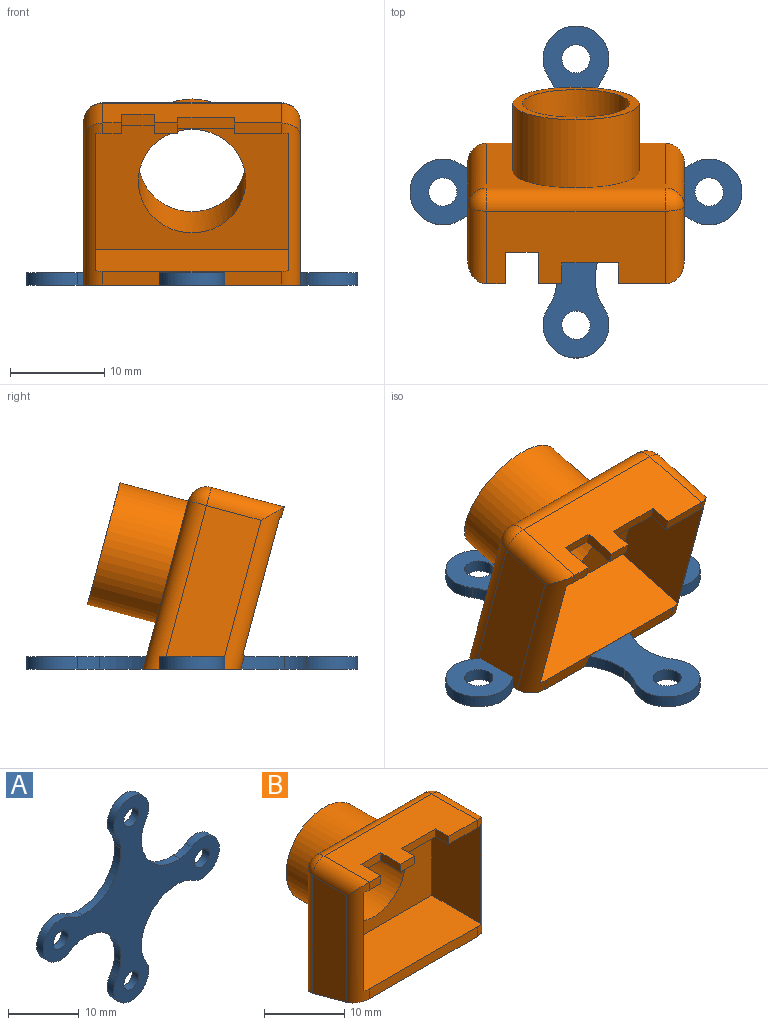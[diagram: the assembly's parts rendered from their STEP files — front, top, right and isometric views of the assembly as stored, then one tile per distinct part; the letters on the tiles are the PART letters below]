
ASSEMBLY  parts=2 mates=1
PART A: 22 faces, bbox 35.3x1.3x35.3 mm
  f0: cylinder r=5mm len=2.39mm, axis (0,1,0), area 3.3mm2, adj f1,f19,f20,f21
  f1: cylinder r=3.5mm len=7mm, axis (0,1,0), area 19.7mm2, adj f0,f2,f20,f21
  f2: cylinder r=5mm len=2.39mm, axis (0,1,0), area 3.3mm2, adj f1,f3,f20,f21
  f3: cylinder r=7.18mm len=7.75mm, axis (0,1,0), area 16.1mm2, adj f2,f4,f20,f21
  f4: cylinder r=5mm len=2.39mm, axis (0,1,0), area 3.3mm2, adj f3,f5,f20,f21
  f5: cylinder r=3.5mm len=7mm, axis (0,1,0), area 19.7mm2, adj f4,f6,f20,f21
  f6: cylinder r=5mm len=2.39mm, axis (0,1,0), area 3.3mm2, adj f5,f7,f20,f21
  f7: cylinder r=7.18mm len=7.75mm, axis (0,1,0), area 16.1mm2, adj f6,f8,f20,f21
  f8: cylinder r=5mm len=2.39mm, axis (0,1,0), area 3.3mm2, adj f7,f9,f20,f21
  f9: cylinder r=3.5mm len=7mm, axis (0,1,0), area 19.7mm2, adj f8,f10,f20,f21
  f10: cylinder r=5mm len=2.39mm, axis (0,1,0), area 3.3mm2, adj f9,f11,f20,f21
  f11: cylinder r=7.18mm len=7.75mm, axis (0,1,0), area 16.1mm2, adj f10,f12,f20,f21
  f12: cylinder r=5mm len=2.39mm, axis (0,1,0), area 3.3mm2, adj f11,f13,f20,f21
  f13: cylinder r=3.5mm len=7mm, axis (0,1,0), area 19.7mm2, adj f12,f14,f20,f21
  f14: cylinder r=5mm len=2.39mm, axis (0,1,0), area 3.3mm2, adj f13,f19,f20,f21
  f15: cylinder r=1.5mm len=3mm, axis (0,1,0), area 12.3mm2, adj f20,f21
  f16: cylinder r=1.5mm len=3mm, axis (0,1,0), area 12.3mm2, adj f20,f21
  f17: cylinder r=1.5mm len=3mm, axis (0,1,0), area 12.3mm2, adj f20,f21
  f18: cylinder r=1.5mm len=3mm, axis (0,1,0), area 12.3mm2, adj f20,f21
  f19: cylinder r=7.18mm len=7.75mm, axis (0,1,0), area 16.1mm2, adj f0,f14,f20,f21
  f20: plane 35.28x35.28mm, normal (0,-1,0), area 333.8mm2, adj f0,f1,f2,f3,f4,f5,f6,f7
  f21: plane 35.28x35.28mm, normal (0,1,0), area 333.8mm2, adj f0,f1,f2,f3,f4,f5,f6,f7
PART B: 32 faces, bbox 23x17.5x20.5 mm
  f0: plane 19x1.52mm, normal (0,-1,0), area 28.9mm2, adj f9,f22,f23,f29
  f1: plane 2x1.2mm, normal (0,-1,0), area 2.4mm2, adj f5,f6,f16,f23
  f2: plane 5x1.2mm, normal (0,-1,0), area 6mm2, adj f5,f6,f19,f29
  f3: plane 17.96x6mm, normal (1,0,0), area 103mm2, adj f22,f28,f29,f31
  f4: plane 2.5x1.2mm, normal (0,-1,0), area 3mm2, adj f5,f6,f17,f21
  f5: plane 19x8mm, normal (0,0,1), area 126mm2, adj f1,f2,f4,f16,f17,f18,f19,f20
  f6: plane 20.6x8.8mm, normal (0,0,-1), area 155.1mm2, adj f1,f2,f4,f10,f11,f12,f16,f17
  f7: plane 17.96x6mm, normal (-1,0,0), area 103mm2, adj f22,f23,f24,f25
  f8: plane 19x18.5mm, normal (0,1,0), area 210.5mm2, adj f14,f22,f25,f27,f28
  f9: plane 20.6x8.8mm, normal (0,0,1), area 181.2mm2, adj f0,f10,f11,f12,f23,f29
  f10: plane 15.1x8.63mm, normal (-1,0,0), area 130.4mm2, adj f6,f9,f12,f29
  f11: plane 15.1x8.63mm, normal (1,0,0), area 130.4mm2, adj f6,f9,f12,f23
  f12: plane 20.6x15.1mm, normal (0,-1,0), area 209mm2, adj f6,f9,f10,f11,f13
  f13: cylinder r=5.7mm len=11.4mm, axis (0,1,0), area 311.6mm2, adj f12,f15
  f14: cylinder r=6.7mm len=13.4mm, axis (0,-1,0), area 315.7mm2, adj f8,f15
  f15: plane 13.4x13.4mm, normal (0,1,0), area 39mm2, adj f13,f14
  f16: plane 3.5x1.2mm, normal (1,0,0), area 4.2mm2, adj f1,f5,f6,f18
  f17: plane 3.5x1.2mm, normal (-1,0,0), area 4.2mm2, adj f4,f5,f6,f18
  f18: plane 3.5x1.2mm, normal (0,-1,0), area 4.2mm2, adj f5,f6,f16,f17
  f19: plane 2.3x1.2mm, normal (-1,0,0), area 2.8mm2, adj f2,f5,f6,f20
  f20: plane 6x1.2mm, normal (0,-1,0), area 7.2mm2, adj f5,f6,f19,f21
  f21: plane 2.3x1.2mm, normal (1,0,0), area 2.8mm2, adj f4,f5,f6,f20
  f22: plane 23x10mm, normal (0,-0.26,-0.97), area 234.6mm2, adj f0,f3,f7,f8,f23,f25,f28,f29
  f23: cylinder r=2mm len=18.36mm, axis (0,0,1), area 41.9mm2, adj f0,f1,f6,f7,f9,f11,f22,f24
  f24: cylinder r=2mm len=8mm, axis (0,-1,0), area 22.8mm2, adj f5,f7,f23,f26
  f25: cylinder r=2mm len=18.5mm, axis (0,0,-1), area 57.5mm2, adj f7,f8,f22,f26
  f26: sphere r=2mm, area 6.3mm2, adj f24,f25,f27
  f27: cylinder r=2mm len=19mm, axis (-1,0,0), area 59.7mm2, adj f5,f8,f26,f30
  f28: cylinder r=2mm len=18.5mm, axis (0,0,1), area 57.5mm2, adj f3,f8,f22,f30
  f29: cylinder r=2mm len=18.36mm, axis (0,0,-1), area 41.9mm2, adj f0,f2,f3,f6,f9,f10,f22,f31
  f30: sphere r=2mm, area 6.3mm2, adj f27,f28,f31
  f31: cylinder r=2mm len=8mm, axis (0,1,0), area 22.8mm2, adj f3,f5,f29,f30
PLACE A rot(axis=(1,0,0),90deg) t=(-0.96,-36.5,11.6)mm
PLACE B rot(axis=(1,0,0),15deg) t=(-0.96,-34.37,21.65)mm
MATE fastened B.f22 <-> A.f20  axis (0,0,-1) through (-0.96,-36.5,10.3)mm
